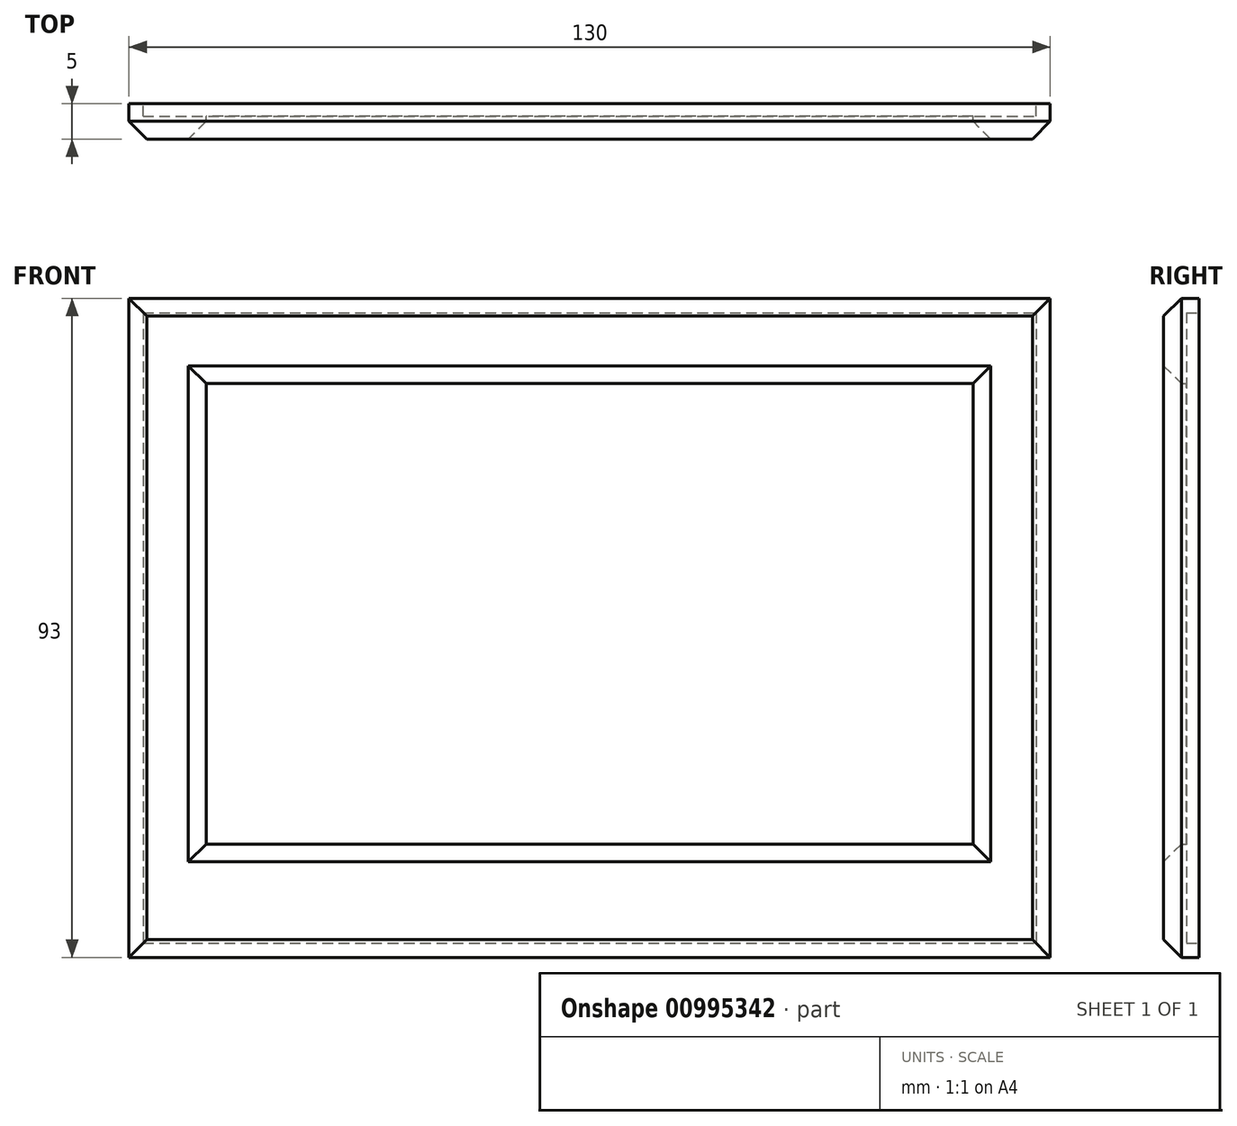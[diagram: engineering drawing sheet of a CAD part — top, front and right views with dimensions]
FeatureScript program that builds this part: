
annotation { "Feature Type Name" : "Feature", "Feature Type Description" : "" }
export const myFeature = defineFeature(function(context is Context, id is Id, definition is map)
    precondition{}
    {
        {
            var Q0;
            Q0=qCreatedBy(makeId("Front.planeOp"),FACE);
            var sketch = newSketch(context, id + "F0", { "sketchPlane" : qUnion([Q0])});
            skPoint(sketch, "E0.middle", {"position": v(0, 0) * mm});
            skLineSegment(sketch, "E1.bottom", {"start": v(-70.6, 37.8) * mm, "end": v(59.4, 37.8) * mm});
            skLineSegment(sketch, "E1.top", {"start": v(-70.6, -55.2) * mm, "end": v(59.4, -55.2) * mm});
            skLineSegment(sketch, "E1.left", {"start": v(-70.6, 37.8) * mm, "end": v(-70.6, -55.2) * mm});
            skLineSegment(sketch, "E1.right", {"start": v(59.4, 37.8) * mm, "end": v(59.4, -55.2) * mm});
            skSolve(sketch);
        }
        {
            var Q0;
            Q0=makeQuery(id+"F0.imprint","IMPRINT",FACE,{"disambiguationData":[TD([[makeQuery(id+"F0.imprint","IMPRINT",EDGE,{"derivedFrom":sQuery(id+"F0.wireOp",EDGE,"E1.bottom")}),-1.0]])]});
            var sketch = newSketch(context, id + "F1", { "sketchPlane" : qUnion([Q0])});
            skLineSegment(sketch, "E2.bottom", {"start": v(-68.6, 35.8) * mm, "end": v(57.4, 35.8) * mm});
            skLineSegment(sketch, "E2.top", {"start": v(-68.6, -53.2) * mm, "end": v(57.4, -53.2) * mm});
            skLineSegment(sketch, "E2.left", {"start": v(-68.6, 35.8) * mm, "end": v(-68.6, -53.2) * mm});
            skLineSegment(sketch, "E2.right", {"start": v(57.4, 35.8) * mm, "end": v(57.4, -53.2) * mm});
            skSolve(sketch);
        }
        {
            var Q0;
            Q0=makeQuery(id+"F0.imprint","IMPRINT",FACE,{"disambiguationData":[TD([[makeQuery(id+"F0.imprint","IMPRINT",EDGE,{"derivedFrom":sQuery(id+"F0.wireOp",EDGE,"E1.bottom")}),-1.0]])]});
            var sketch = newSketch(context, id + "F2", { "sketchPlane" : qUnion([Q0])});
            skLineSegment(sketch, "E3.bottom", {"start": v(-59.7, 25.8) * mm, "end": v(48.5, 25.8) * mm});
            skLineSegment(sketch, "E3.top", {"start": v(-59.7, -39.2) * mm, "end": v(48.5, -39.2) * mm});
            skLineSegment(sketch, "E3.left", {"start": v(-59.7, 25.8) * mm, "end": v(-59.7, -39.2) * mm});
            skLineSegment(sketch, "E3.right", {"start": v(48.5, 25.8) * mm, "end": v(48.5, -39.2) * mm});
            skSolve(sketch);
        }
        {
            var Q0;
            Q0 = qSketchRegion(id + "F0", true);
            extrude(context, id + "F3", {"entities" : qUnion([Q0]), "depth" : 5 * mm, "offsetDistance" : 25 * mm});
        }
        {
            var Q0;
            Q0 = qSketchRegion(id + "F1", true);
            extrude(context, id + "F4", {"entities" : qUnion([Q0]), "operationType" : NewBodyOperationType.REMOVE, "depth" : 1.8 * mm, "offsetDistance" : 25 * mm});
        }
        {
            var Q0;
            Q0 = qSketchRegion(id + "F2", true);
            extrude(context, id + "F5", {"entities" : qUnion([Q0]), "operationType" : NewBodyOperationType.REMOVE, "depth" : 25 * mm, "offsetDistance" : 25 * mm});
        }
        {
            var Q0;
            Q0=makeQuery(id+"F5.boolean.opBoolean","INTERSECT",EDGE,{"derivedFrom":[makeQuery(id+"F3.opExtrude","CAP_FACE",FACE,{"disambiguationData":[OSD([sQuery(id+"F0.wireOp",EDGE,"E1.bottom"),sQuery(id+"F0.wireOp",EDGE,"E1.top"),sQuery(id+"F0.wireOp",EDGE,"E1.left"),sQuery(id+"F0.wireOp",EDGE,"E1.right")])],"isStart":false}),makeQuery(id+"F5.opExtrude","SWEPT_FACE",FACE,{"disambiguationData":[OSD([sQuery(id+"F2.wireOp",EDGE,"E3.bottom")])]})]});
            var Q1;
            Q1=makeQuery(id+"F5.boolean.opBoolean","INTERSECT",EDGE,{"derivedFrom":[makeQuery(id+"F3.opExtrude","CAP_FACE",FACE,{"disambiguationData":[OSD([sQuery(id+"F0.wireOp",EDGE,"E1.bottom"),sQuery(id+"F0.wireOp",EDGE,"E1.top"),sQuery(id+"F0.wireOp",EDGE,"E1.left"),sQuery(id+"F0.wireOp",EDGE,"E1.right")])],"isStart":false}),makeQuery(id+"F5.opExtrude","SWEPT_FACE",FACE,{"disambiguationData":[OSD([sQuery(id+"F2.wireOp",EDGE,"E3.left")])]})]});
            var Q2;
            Q2=makeQuery(id+"F5.boolean.opBoolean","INTERSECT",EDGE,{"derivedFrom":[makeQuery(id+"F3.opExtrude","CAP_FACE",FACE,{"disambiguationData":[OSD([sQuery(id+"F0.wireOp",EDGE,"E1.bottom"),sQuery(id+"F0.wireOp",EDGE,"E1.top"),sQuery(id+"F0.wireOp",EDGE,"E1.left"),sQuery(id+"F0.wireOp",EDGE,"E1.right")])],"isStart":false}),makeQuery(id+"F5.opExtrude","SWEPT_FACE",FACE,{"disambiguationData":[OSD([sQuery(id+"F2.wireOp",EDGE,"E3.right")])]})]});
            var Q3;
            Q3=makeQuery(id+"F5.boolean.opBoolean","INTERSECT",EDGE,{"derivedFrom":[makeQuery(id+"F3.opExtrude","CAP_FACE",FACE,{"disambiguationData":[OSD([sQuery(id+"F0.wireOp",EDGE,"E1.bottom"),sQuery(id+"F0.wireOp",EDGE,"E1.top"),sQuery(id+"F0.wireOp",EDGE,"E1.left"),sQuery(id+"F0.wireOp",EDGE,"E1.right")])],"isStart":false}),makeQuery(id+"F5.opExtrude","SWEPT_FACE",FACE,{"disambiguationData":[OSD([sQuery(id+"F2.wireOp",EDGE,"E3.top")])]})]});
            var Q4;
            Q4=makeQuery(id+"F3.opExtrude","CAP_EDGE",EDGE,{"disambiguationData":[OSD([sQuery(id+"F0.wireOp",EDGE,"E1.left")])],"isStart":false});
            var Q5;
            Q5=makeQuery(id+"F3.opExtrude","CAP_EDGE",EDGE,{"disambiguationData":[OSD([sQuery(id+"F0.wireOp",EDGE,"E1.top")])],"isStart":false});
            var Q6;
            Q6=makeQuery(id+"F3.opExtrude","CAP_EDGE",EDGE,{"disambiguationData":[OSD([sQuery(id+"F0.wireOp",EDGE,"E1.bottom")])],"isStart":false});
            var Q7;
            Q7=makeQuery(id+"F3.opExtrude","CAP_EDGE",EDGE,{"disambiguationData":[OSD([sQuery(id+"F0.wireOp",EDGE,"E1.right")])],"isStart":false});
            chamfer(context, id + "F6", {"entities" : qUnion([Q0, Q1, Q2, Q3, Q4, Q5, Q6, Q7]), "width" : 2.5 * mm, "tangentPropagation" : true});
        }
    });
